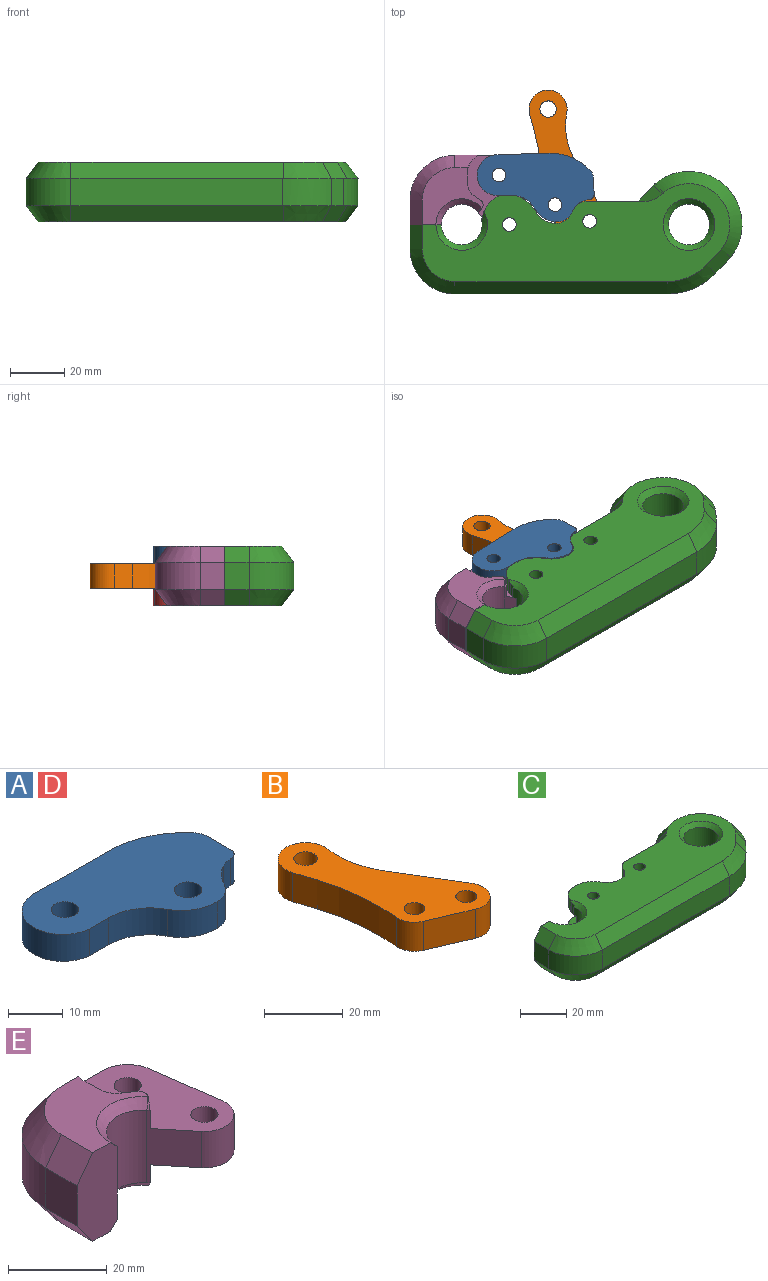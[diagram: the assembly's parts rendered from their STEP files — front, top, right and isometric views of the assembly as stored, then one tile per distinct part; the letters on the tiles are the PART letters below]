
ASSEMBLY  parts=5 mates=6
PART A: 17 faces, bbox 42.8x25.3x6 mm
  f0: plane 19.12x6mm, normal (0,1,0), area 114.7mm2, adj f1,f14,f15,f16
  f1: cylinder r=7.5mm len=14.97mm, axis (0,0,-1), area 137.3mm2, adj f0,f2,f15,f16
  f2: plane 6x4.98mm, normal (0,-1,0), area 29.9mm2, adj f1,f3,f15,f16
  f3: cylinder r=10.73mm len=9.45mm, axis (0,0,-1), area 69.3mm2, adj f2,f4,f15,f16
  f4: cylinder r=9.01mm len=8.17mm, axis (0,0,-1), area 59.6mm2, adj f3,f5,f15,f16
  f5: cylinder r=5.59mm len=6mm, axis (0,0,-1), area 35.9mm2, adj f4,f6,f15,f16
  f6: cylinder r=9.99mm len=6mm, axis (0,0,-1), area 34.6mm2, adj f5,f7,f15,f16
  f7: cylinder r=5mm len=6mm, axis (0,0,-1), area 15.6mm2, adj f6,f8,f15,f16
  f8: plane 6x0.13mm, normal (0,-1,0), area 0.8mm2, adj f7,f9,f15,f16
  f9: cylinder r=2mm len=6mm, axis (0,0,-1), area 18.8mm2, adj f8,f10,f15,f16
  f10: plane 6x5.8mm, normal (1,0,0), area 34.8mm2, adj f9,f11,f15,f16
  f11: cylinder r=4.48mm len=6mm, axis (0,0,-1), area 19.6mm2, adj f10,f14,f15,f16
  f12: cylinder r=2.5mm len=6mm, axis (0,0,-1), area 94.2mm2, adj f15,f16
  f13: cylinder r=2.5mm len=6mm, axis (0,0,-1), area 94.2mm2, adj f15,f16
  f14: cylinder r=20.14mm len=15.03mm, axis (0,0,-1), area 101.8mm2, adj f0,f11,f15,f16
  f15: plane 42.78x25.34mm, normal (0,0,1), area 702.9mm2, adj f0,f1,f2,f3,f4,f5,f6,f7
  f16: plane 42.78x25.34mm, normal (0,0,-1), area 702.9mm2, adj f0,f1,f2,f3,f4,f5,f6,f7
PART B: 13 faces, bbox 30x53.6x9 mm
  f0: cylinder r=6mm len=9mm, axis (0,0,-1), area 68.8mm2, adj f1,f5,f6,f9
  f1: plane 13x9mm, normal (-0.39,-0.92,0), area 127.2mm2, adj f0,f3,f5,f6
  f2: cylinder r=2.65mm len=9mm, axis (0,0,-1), area 149.9mm2, adj f5,f6
  f3: cylinder r=6mm len=9.11mm, axis (0,0,-1), area 136mm2, adj f1,f5,f6,f7
  f4: cylinder r=2.65mm len=9mm, axis (0,0,-1), area 149.9mm2, adj f5,f6
  f5: plane 53.55x30mm, normal (0,0,1), area 724mm2, adj f0,f1,f2,f3,f4,f7,f8,f9
  f6: plane 53.55x30mm, normal (0,0,-1), area 724mm2, adj f0,f1,f2,f3,f4,f7,f8,f9
  f7: plane 19.47x11.78mm, normal (0.86,0.52,0), area 204.8mm2, adj f3,f5,f6,f8
  f8: cylinder r=25.6mm len=16.96mm, axis (0,0,-1), area 158.8mm2, adj f5,f6,f7,f10
  f9: cylinder r=62.26mm len=25.68mm, axis (0,0,-1), area 234mm2, adj f0,f5,f6,f11
  f10: cylinder r=7mm len=14mm, axis (0,0,-1), area 226.6mm2, adj f5,f6,f8,f11
  f11: plane 9x6.54mm, normal (-0.95,-0.31,0), area 61.8mm2, adj f5,f6,f9,f10
  f12: cylinder r=3mm len=9mm, axis (0,0,-1), area 169.6mm2, adj f5,f6
PART C: 79 faces, bbox 123.9x46.9x23.8 mm
  f0: plane 21.56x6mm, normal (0,1,0), area 126.6mm2, adj f1,f2,f41,f53,f54,f78
  f1: plane 3.71x3.54mm, normal (0,0,-1), area 0.1mm2, adj f0,f35,f78
  f2: cylinder r=8.81mm len=6.41mm, axis (0,0,1), area 13.2mm2, adj f0,f53,f78
  f3: cylinder r=8.81mm len=6.41mm, axis (0,0,-1), area 13.2mm2, adj f13,f27,f77
  f4: plane 3.71x3.54mm, normal (0,0,1), area 0.1mm2, adj f13,f35,f77
  f5: plane 36.32x10mm, normal (0,1,0), area 363.2mm2, adj f28,f35,f54,f75
  f6: cylinder r=5mm len=6mm, axis (0,0,-1), area 18.4mm2, adj f7,f26,f27,f28
  f7: cylinder r=11mm len=6mm, axis (0,0,-1), area 36.9mm2, adj f6,f8,f27,f28
  f8: cylinder r=5mm len=6mm, axis (0,0,-1), area 7.4mm2, adj f7,f9,f27,f28,f71
  f9: cylinder r=22.86mm len=5.14mm, axis (0,0,-1), area 7.3mm2, adj f8,f10,f28,f71
  f10: plane 4.49x0.5mm, normal (0,1,0), area 2.1mm2, adj f9,f11,f28,f71
  f11: cylinder r=7.5mm len=18mm, axis (0,0,-1), area 442.6mm2, adj f10,f12,f28,f40,f54,f71,f72,f76
  f12: plane 22x11.5mm, normal (0,1,0), area 222mm2, adj f11,f27,f29,f53,f58,f66,f71,f72
  f13: plane 21.56x6mm, normal (0,1,0), area 126.6mm2, adj f3,f4,f14,f27,f28,f77
  f14: cylinder r=5mm len=6mm, axis (0,0,-1), area 21.5mm2, adj f13,f15,f27,f28
  f15: cylinder r=7.23mm len=6mm, axis (0,0,-1), area 22.6mm2, adj f14,f16,f27,f28
  f16: cylinder r=5mm len=6mm, axis (0,0,-1), area 4.3mm2, adj f15,f17,f27,f28
  f17: cylinder r=5.87mm len=6mm, axis (0,0,-1), area 35.1mm2, adj f16,f18,f27,f28
  f18: cylinder r=5mm len=6mm, axis (0,0,-1), area 2.2mm2, adj f17,f19,f27,f28
  f19: cylinder r=9mm len=6.51mm, axis (0,0,-1), area 43.2mm2, adj f18,f20,f27,f28
  f20: cylinder r=5mm len=6mm, axis (0,0,-1), area 8.3mm2, adj f19,f21,f27,f28
  f21: cylinder r=15.44mm len=6.1mm, axis (0,0,-1), area 51.8mm2, adj f20,f22,f27,f28
  f22: cylinder r=5mm len=6mm, axis (0,0,-1), area 14.8mm2, adj f21,f26,f27,f28
  f23: cylinder r=2.5mm len=6mm, axis (0,0,-1), area 94.2mm2, adj f27,f28
  f24: cylinder r=2.5mm len=6mm, axis (0,0,-1), area 94.2mm2, adj f27,f28
  f25: cylinder r=7.5mm len=18mm, axis (0,0,-1), area 848.2mm2, adj f73,f74
  f26: plane 6x4.3mm, normal (0,1,0), area 25.8mm2, adj f6,f22,f27,f28
  f27: plane 113.03x36.03mm, normal (0,0,1), area 2539mm2, adj f3,f6,f7,f8,f12,f13,f14,f15
  f28: plane 57.61x18.57mm, normal (0,0,-1), area 662.3mm2, adj f5,f6,f7,f8,f9,f10,f11,f13
  f29: plane 10x9mm, normal (-1,0,0), area 90mm2, adj f12,f30,f58,f66
  f30: cylinder r=16.5mm len=16.5mm, axis (0,0,1), area 259.2mm2, adj f29,f31,f59,f67
  f31: plane 77.79x10mm, normal (0,-1,0), area 777.9mm2, adj f30,f32,f60,f68
  f32: cylinder r=25mm len=18.1mm, axis (0,0,1), area 202.4mm2, adj f31,f33,f60,f61,f62,f68,f69,f70
  f33: plane 10x4.36mm, normal (0.72,-0.69,0), area 60.3mm2, adj f32,f34,f62,f70
  f34: cylinder r=19.4mm len=33.44mm, axis (0,0,1), area 609.4mm2, adj f33,f35,f55,f63
  f35: plane 21.38x20.36mm, normal (-0.72,0.69,0), area 295.2mm2, adj f1,f4,f5,f28,f34,f54,f55,f63
  f36: cylinder r=5mm len=6mm, axis (0,0,1), area 18.4mm2, adj f37,f52,f53,f54
  f37: cylinder r=11mm len=6mm, axis (0,0,1), area 36.9mm2, adj f36,f38,f53,f54
  f38: cylinder r=5mm len=6mm, axis (0,0,1), area 7.4mm2, adj f37,f39,f53,f54,f72
  f39: cylinder r=22.86mm len=5.14mm, axis (0,0,1), area 7.3mm2, adj f38,f40,f54,f72
  f40: plane 4.49x0.5mm, normal (0,1,0), area 2.1mm2, adj f11,f39,f54,f72
  f41: cylinder r=5mm len=6mm, axis (0,0,1), area 21.5mm2, adj f0,f42,f53,f54
  f42: cylinder r=7.23mm len=6mm, axis (0,0,1), area 22.6mm2, adj f41,f43,f53,f54
  f43: cylinder r=5mm len=6mm, axis (0,0,1), area 4.3mm2, adj f42,f44,f53,f54
  f44: cylinder r=5.87mm len=6mm, axis (0,0,1), area 35.1mm2, adj f43,f45,f53,f54
  f45: cylinder r=5mm len=6mm, axis (0,0,1), area 2.2mm2, adj f44,f46,f53,f54
  f46: cylinder r=9mm len=6.51mm, axis (0,0,1), area 43.2mm2, adj f45,f47,f53,f54
  f47: cylinder r=5mm len=6mm, axis (0,0,1), area 8.3mm2, adj f46,f48,f53,f54
  f48: cylinder r=15.44mm len=6.1mm, axis (0,0,1), area 51.8mm2, adj f47,f49,f53,f54
  f49: cylinder r=5mm len=6mm, axis (0,0,1), area 14.8mm2, adj f48,f52,f53,f54
  f50: cylinder r=2.5mm len=6mm, axis (0,0,1), area 94.2mm2, adj f53,f54
  f51: cylinder r=2.5mm len=6mm, axis (0,0,1), area 94.2mm2, adj f53,f54
  f52: plane 6x4.3mm, normal (0,1,0), area 25.8mm2, adj f36,f49,f53,f54
  f53: plane 113.11x36.1mm, normal (0,0,-1), area 2538.4mm2, adj f0,f2,f12,f36,f37,f38,f41,f42
  f54: plane 57.61x18.57mm, normal (0,0,1), area 662.3mm2, adj f0,f5,f11,f35,f36,f37,f38,f39
  f55: plane 34.71x32.92mm, normal (0,0,1), area 6.1mm2, adj f34,f35,f56,f57,f62,f78
  f56: bspline ~31.8x31.6mm, area 374.7mm2, adj f53,f55,f57,f62
  f57: cone r=9.5mm half-angle=36.9deg, axis (0,0,1), area 7.6mm2, adj f53,f55,f56,f78
  f58: plane 9x6mm, normal (-0.8,0,-0.6), area 67.5mm2, adj f12,f29,f53,f59
  f59: cone r=16.5mm half-angle=36.9deg, axis (0,0,1), area 167.9mm2, adj f30,f53,f58,f60
  f60: plane 78x6mm, normal (0,-0.8,-0.6), area 585mm2, adj f31,f32,f53,f59,f61
  f61: cone r=24.5mm half-angle=36.9deg, axis (0,0,1), area 135.1mm2, adj f32,f53,f60,f62
  f62: plane 8.97x8.9mm, normal (0.58,-0.55,-0.6), area 61mm2, adj f32,f33,f53,f55,f56,f61
  f63: plane 34.71x32.92mm, normal (0,0,-1), area 6.1mm2, adj f34,f35,f64,f65,f70,f77
  f64: bspline ~31.8x31.6mm, area 374.7mm2, adj f27,f63,f65,f70
  f65: cone r=5mm half-angle=36.9deg, axis (0,0,-1), area 7.6mm2, adj f27,f63,f64,f77
  f66: plane 9x6mm, normal (-0.8,0,0.6), area 67.5mm2, adj f12,f27,f29,f67
  f67: cone r=12mm half-angle=36.9deg, axis (0,0,-1), area 167.9mm2, adj f27,f30,f66,f68
  f68: plane 78x6mm, normal (0,-0.8,0.6), area 585mm2, adj f27,f31,f32,f67,f69
  f69: cone r=20mm half-angle=36.9deg, axis (0,0,-1), area 135.1mm2, adj f27,f32,f68,f70
  f70: plane 8.97x8.9mm, normal (0.58,-0.55,0.6), area 61mm2, adj f27,f32,f33,f63,f64,f69
  f71: cone r=7.5mm half-angle=45deg, axis (0,0,1), area 85.1mm2, adj f8,f9,f10,f11,f12,f27
  f72: cone r=9.5mm half-angle=45deg, axis (0,0,-1), area 85.1mm2, adj f11,f12,f38,f39,f40,f53
  f73: cone r=7.5mm half-angle=45deg, axis (0,0,1), area 151.1mm2, adj f25,f27
  f74: cone r=9.5mm half-angle=45deg, axis (0,0,-1), area 151.1mm2, adj f25,f53
  f75: plane 10x8.12mm, normal (0.88,0.48,0), area 92.7mm2, adj f5,f28,f54,f76
  f76: plane 10x0.8mm, normal (0,1,0), area 8mm2, adj f11,f28,f54,f75
  f77: plane 10.56x7.76mm, normal (-0.58,0.55,0.6), area 41.3mm2, adj f3,f4,f13,f63,f65
  f78: plane 10.56x7.76mm, normal (-0.58,0.55,-0.6), area 41.3mm2, adj f0,f1,f2,f55,f57
PART D: same geometry as A
PART E: 37 faces, bbox 42.5x31.5x22 mm
  f0: plane 8.7x6mm, normal (0,0.8,-0.6), area 47.6mm2, adj f1,f8,f13,f31
  f1: cylinder r=8.13mm len=7.63mm, axis (0,0,-1), area 39.8mm2, adj f0,f3,f8,f13,f14
  f2: plane 31.5x21.48mm, normal (0,0,1), area 438.8mm2, adj f4,f5,f6,f7,f8,f19,f20,f21
  f3: plane 31.5x21.48mm, normal (0,0,-1), area 438.8mm2, adj f1,f4,f5,f6,f7,f8,f14,f15
  f4: plane 18x8.59mm, normal (-0.77,-0.64,0), area 106mm2, adj f2,f3,f5,f12,f18,f19,f34,f36
  f5: cylinder r=6mm len=10.63mm, axis (0,0,-1), area 139.7mm2, adj f2,f3,f4,f6
  f6: plane 18.38x9mm, normal (0.99,0.14,0), area 166.9mm2, adj f2,f3,f5,f7
  f7: cylinder r=7.3mm len=9mm, axis (0,0,-1), area 94.3mm2, adj f2,f3,f6,f8
  f8: plane 16.2x10mm, normal (0,1,0), area 154.5mm2, adj f0,f1,f2,f3,f7,f9,f29,f32
  f9: cylinder r=16.5mm len=16.5mm, axis (0,0,-1), area 259.2mm2, adj f8,f10,f28,f31
  f10: plane 10x9mm, normal (-1,0,0), area 90mm2, adj f9,f11,f27,f30
  f11: plane 22x11.5mm, normal (0,-1,0), area 222mm2, adj f10,f12,f13,f24,f27,f30,f33,f35
  f12: cylinder r=7.5mm len=18mm, axis (0,0,-1), area 331mm2, adj f4,f11,f33,f35
  f13: plane 22.35x21mm, normal (0,0,-1), area 242.3mm2, adj f0,f1,f11,f14,f15,f16,f17,f18
  f14: plane 6.5x3.57mm, normal (1,0.07,0), area 23.3mm2, adj f1,f3,f13,f15
  f15: cylinder r=4.54mm len=6.5mm, axis (0,0,-1), area 26.3mm2, adj f3,f13,f14,f16
  f16: plane 6.5x2.81mm, normal (0.58,0.82,0), area 22.3mm2, adj f3,f13,f15,f17
  f17: cylinder r=2mm len=6.5mm, axis (0,0,-1), area 20.4mm2, adj f3,f13,f16,f18
  f18: plane 6.5x1.84mm, normal (0.82,-0.58,0), area 12.5mm2, adj f3,f4,f13,f17,f34
  f19: plane 6.5x1.84mm, normal (0.82,-0.58,0), area 12.5mm2, adj f2,f4,f20,f24,f36
  f20: cylinder r=2mm len=6.5mm, axis (0,0,-1), area 20.4mm2, adj f2,f19,f21,f24
  f21: plane 6.5x2.81mm, normal (0.58,0.82,0), area 22.3mm2, adj f2,f20,f22,f24
  f22: cylinder r=4.54mm len=6.5mm, axis (0,0,-1), area 26.3mm2, adj f2,f21,f23,f24
  f23: plane 6.5x3.57mm, normal (1,0.07,0), area 23.3mm2, adj f2,f22,f24,f32
  f24: plane 22.35x21mm, normal (0,0,1), area 242.3mm2, adj f11,f19,f20,f21,f22,f23,f27,f28
  f25: cylinder r=2.75mm len=9mm, axis (0,0,-1), area 155.5mm2, adj f2,f3
  f26: cylinder r=2.75mm len=9mm, axis (0,0,-1), area 155.5mm2, adj f2,f3
  f27: plane 9x6mm, normal (-0.8,0,0.6), area 67.5mm2, adj f10,f11,f24,f28
  f28: cone r=16.5mm half-angle=36.9deg, axis (0,0,-1), area 167.9mm2, adj f9,f24,f27,f29
  f29: plane 8.7x6mm, normal (0,0.8,0.6), area 47.6mm2, adj f8,f24,f28,f32
  f30: plane 9x6mm, normal (-0.8,0,-0.6), area 67.5mm2, adj f10,f11,f13,f31
  f31: cone r=12mm half-angle=36.9deg, axis (0,0,1), area 167.9mm2, adj f0,f9,f13,f30
  f32: cylinder r=8.13mm len=7.63mm, axis (0,0,-1), area 39.8mm2, adj f2,f8,f23,f24,f29
  f33: cone r=9.5mm half-angle=45deg, axis (0,0,-1), area 58.9mm2, adj f11,f12,f13,f34
  f34: plane 2x1.77mm, normal (-0.55,-0.45,-0.71), area 1mm2, adj f4,f13,f18,f33
  f35: cone r=7.5mm half-angle=45deg, axis (0,0,1), area 58.9mm2, adj f11,f12,f24,f36
  f36: plane 2x1.77mm, normal (-0.55,-0.45,0.71), area 1mm2, adj f4,f19,f24,f35
PLACE A rot(axis=(0,0,1),1.5deg) t=(0.43,0.1,3)mm
PLACE B rot(axis=(0,0,-1),2.4deg) t=(-0.02,1.24,-5)mm
PLACE C at identity fixed
PLACE D rot(axis=(0,0,1),1.5deg) t=(0.43,0.1,-13)mm
PLACE E rot(axis=(0,0,1),0.2deg) t=(0,0,-5)mm
MATE planar D.f0 <-> A.f0  axis (-0.03,1,0) through (4.99,25.93,-10)mm
MATE revolute A.f12 <-> E.f7  axis (0,0,-1) through (-3.86,18.19,0)mm
MATE revolute A.f13 <-> B.f0  axis (0,0,-1) through (16.74,7.29,0)mm
MATE revolute C.f23 <-> B.f2  axis (0,0,-1) through (29.5,1.2,0)mm
MATE revolute E.f26 <-> C.f24  axis (0,0,-1) through (0,0,-0.5)mm
MATE revolute E.f7 <-> D.f12  axis (0,0,-1) through (-3.86,18.19,-9.5)mm
